# Revit family: Accessories-Teknion-HWBANP_hiSpace_Workstation_Name_Plate-R2020
name_source: partatom
category: Furniture
units: mm (PartAtom-declared; Revit-internal decimal feet)

## family parameters
Always vertical = Yes
Cut with Voids When Loaded = No
OmniClass Number = 23.40.20.00
OmniClass Title = General Furniture and Specialties
Room Calculation Point = No
Shared = Yes
Work Plane-Based = No

## types (6) — shared parameters
Assembly Code = E2020200
Manufacturer = Teknion
Manufacturer Fax = 416.661.4586
Part Number = HWBANP
Product Documentation Link = https://www.teknion.com
Product Line = hiSpace Universal Components
Product Page URL = https://www.teknion.com
Series = Height-Adjustable Bench hiSpace
Sustainability Data = https://www.teknion.com
URL = www.teknion.com
Unit Weight URL = http://www.teknion.com
Warranty = http://www.teknion.com
zero-valued in all types: Default Elevation

## per-type parameters (varying)
| type | Bracket Lenght | Description | Double Sided (D) | Infinity option | Model | No Infinity Option | Screen Height | Screen Size | Single Sided (S) |
| Solid Screen, Hang-on Single-Sided | 1 " | hiSpace Workstation Name Plate, Solid Screen, Hang-on Single-Sided | No | No | HWBANPSS | Yes | 0.122 " | 0.929 " | Yes |
| Solid Screen, Hang-on Double-Sided | 2.294 " | hiSpace Workstation Name Plate ,Solid Screen, Hang-on Double-Sided | Yes | No | HWBANPSD | Yes | 0.122 " | 0.929 " | No |
| Frame Fabric Screen, Hang-on Single-Sided | 1 " | hiSpace Workstation Name Plate, Frame Fabric Screen, Hang-on Single-Sided | No | No | HWBANPFS | Yes | 0.122 " | 0.929 " | Yes |
| Frame Fabric Screen, Hang-on Double-Sided | 2.294 " | hiSpace Workstation Name Plate, Frame Fabric Screen, Hang-on Double-Sided | Yes | No | HWBANPFD | Yes | 0.122 " | 0.929 " | No |
| Infinity Screen, Hang-on Single-Sided | 1 " | hiSpace Workstation Name Plate, Infinity Screen, Hang-on Single-Sided | No | Yes | HWBANPIS | No | 1.103 " | 0.64 " | Yes |
| Smooth Felt, Hang-on Single-Sided | 1 " | hiSpace Workstation Name Plate,Smooth Felt, Hang-on Single-Sided | No | No | HWBANPDS | Yes | 0.076 " | 0.645 " | Yes |

## geometry (parser evidence)
native form markers: Sweep x3
no freeform markers — native parametric forms only
